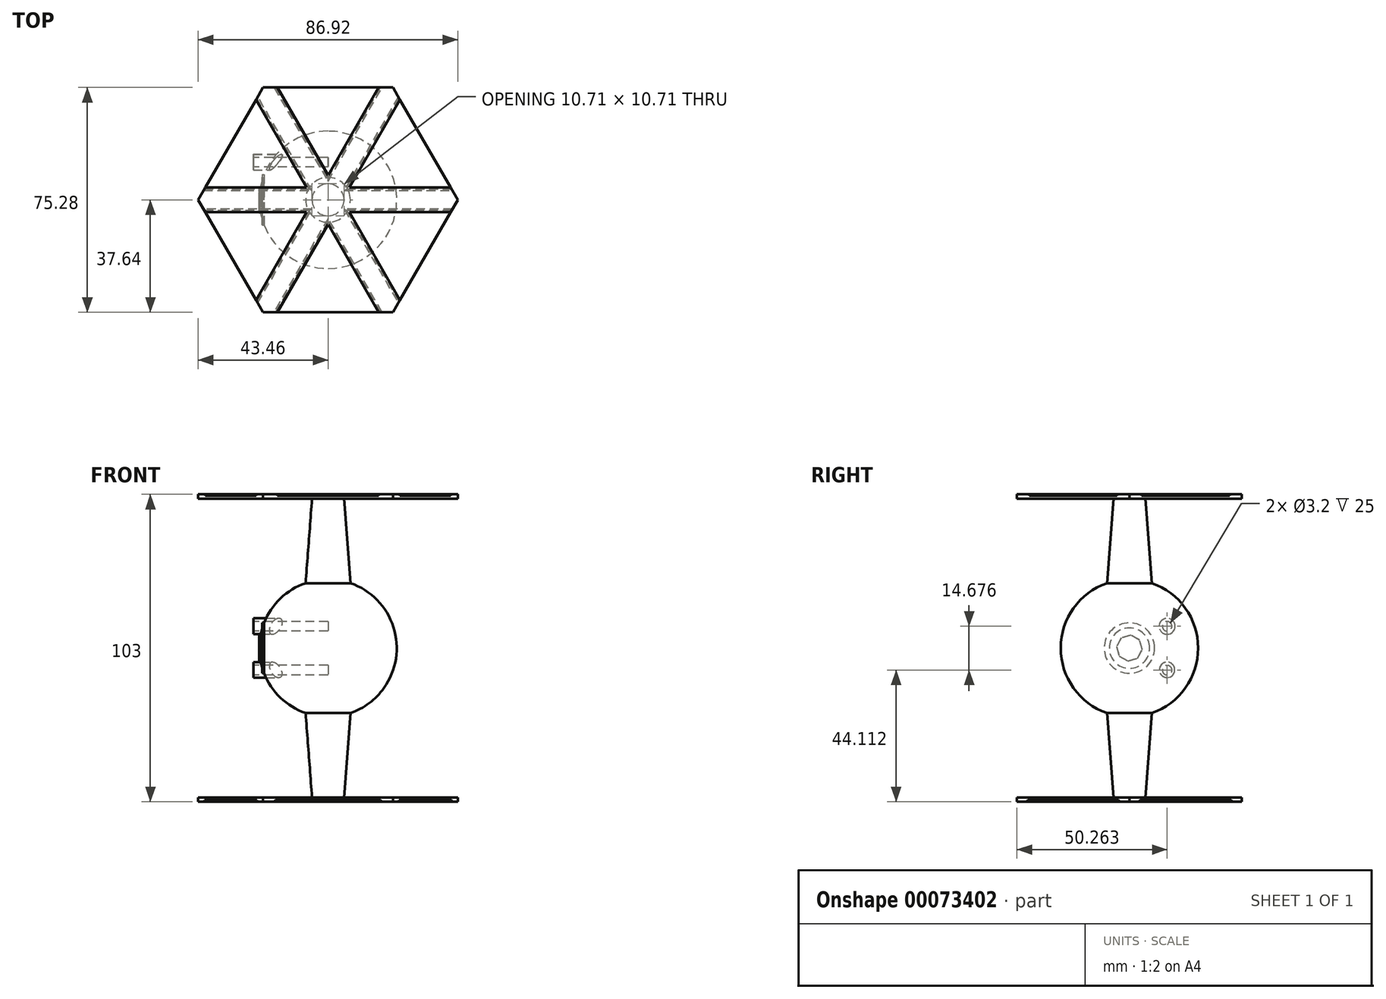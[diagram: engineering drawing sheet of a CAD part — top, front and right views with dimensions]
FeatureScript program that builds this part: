
annotation { "Feature Type Name" : "Feature", "Feature Type Description" : "" }
export const myFeature = defineFeature(function(context is Context, id is Id, definition is map)
    precondition{}
    {
        {
            var Q0;
            Q0=qCreatedBy(makeId("Top.planeOp"),FACE);
            var sketch = newSketch(context, id + "F0", { "sketchPlane" : qUnion([Q0])});
            skArc(sketch, "E0", {"start": v(0, -23.02) * mm, "mid": v(23.02, 0) * mm, "end": v(0, 23.02) * mm});
            skPoint(sketch, "E1.start.orphan", {"position": v(0, 24.97) * mm});
            skLineSegment(sketch, "E2", {"start": v(0, 24.97) * mm, "end": v(0, -23.02) * mm});
            skSolve(sketch);
        }
        {
            var Q0;
            Q0 = qSketchRegion(id + "F0", true);
            var Q1;
            Q1=sQuery(id+"F0.wireOp",EDGE,"E2");
            revolve(context, id + "F1", {"entities" : qUnion([Q0]), "axis" : qUnion([Q1]), "revolveType" : RevolveType.ONE_DIRECTION, "angle" : 180 * degree});
        }
        {
            var Q0;
            Q0=qCreatedBy(makeId("Top.planeOp"),FACE);
            var sketch = newSketch(context, id + "F2", { "sketchPlane" : qUnion([Q0])});
            skCircle(sketch, "E3", {"center": v(0, 0) * mm, "radius": 9.16 * mm});
            skSolve(sketch);
        }
        {
            var Q0;
            Q0=qCreatedBy(makeId("Top.planeOp"),FACE);
            cPlane(context, id + "F3", {"entities" : qUnion([Q0]), "cplaneType" : CPlaneType.OFFSET, "offset" : 50 * mm, "width" : 152.4 * mm, "height" : 152.4 * mm});
        }
        {
            var Q0;
            Q0=qCreatedBy(id+"F3.planeOp",FACE);
            var sketch = newSketch(context, id + "F4", { "sketchPlane" : qUnion([Q0])});
            skCircle(sketch, "E4", {"center": v(0, 0) * mm, "radius": 5.35 * mm});
            skSolve(sketch);
        }
        {
            var Q1;
            Q1=makeQuery(id+"F4.imprint","IMPRINT",FACE,{"disambiguationData":[TD([[makeQuery(id+"F4.imprint","IMPRINT",EDGE,{"derivedFrom":sQuery(id+"F4.wireOp",EDGE,"E4")}),1.0]])]});
            var Q2;
            Q2 = qSketchRegion(id + "F2", true);
            loft(context, id + "F5", {"operationType" : NewBodyOperationType.ADD, "sheetProfilesArray" : [{ "sheetProfileEntities" : qUnion([Q1]) }, { "sheetProfileEntities" : qUnion([Q2]) }]});
        }
        {
            var Q0;
            Q0=qCreatedBy(id+"F3.planeOp",FACE);
            var sketch = newSketch(context, id + "F6", { "sketchPlane" : qUnion([Q0])});
            skCircle(sketch, "E5.cCircle", {"center": v(0, 0) * mm, "radius": 37.64 * mm, "construction": true});
            skLineSegment(sketch, "E5.0", {"start": v(21.73, -37.64) * mm, "end": v(-21.73, -37.64) * mm});
            skLineSegment(sketch, "E5.1", {"start": v(-21.73, -37.64) * mm, "end": v(-43.46, 0) * mm});
            skLineSegment(sketch, "E5.2", {"start": v(-43.46, 0) * mm, "end": v(-21.73, 37.64) * mm});
            skLineSegment(sketch, "E5.3", {"start": v(-21.73, 37.64) * mm, "end": v(21.73, 37.64) * mm});
            skLineSegment(sketch, "E5.4", {"start": v(21.73, 37.64) * mm, "end": v(43.46, 0) * mm});
            skLineSegment(sketch, "E5.5", {"start": v(43.46, 0) * mm, "end": v(21.73, -37.64) * mm});
            skPoint(sketch, "E5.0.midPoint", {"position": v(0, -37.64) * mm});
            skSolve(sketch);
        }
        {
            var Q0;
            Q0 = qSketchRegion(id + "F6", true);
            extrude(context, id + "F7", {"entities" : qUnion([Q0]), "operationType" : NewBodyOperationType.ADD, "depth" : 1 * mm});
        }
        {
            var Q0;
            Q0=makeQuery(id+"F7.opExtrude","CAP_FACE",FACE,{"disambiguationData":[OSD([sQuery(id+"F6.wireOp",EDGE,"E5.0"),sQuery(id+"F6.wireOp",EDGE,"E5.1"),sQuery(id+"F6.wireOp",EDGE,"E5.2"),sQuery(id+"F6.wireOp",EDGE,"E5.3"),sQuery(id+"F6.wireOp",EDGE,"E5.4"),sQuery(id+"F6.wireOp",EDGE,"E5.5")])],"isStart":false});
            var sketch = newSketch(context, id + "F8", { "sketchPlane" : qUnion([Q0])});
            skCircle(sketch, "E6.cCircle", {"center": v(0, 0) * mm, "radius": 8.23 * mm, "construction": true});
            skLineSegment(sketch, "E6.0", {"start": v(4.75, -8.23) * mm, "end": v(-4.75, -8.23) * mm});
            skLineSegment(sketch, "E6.1", {"start": v(-4.75, -8.23) * mm, "end": v(-9.5, 0) * mm});
            skLineSegment(sketch, "E6.2", {"start": v(-9.5, 0) * mm, "end": v(-4.75, 8.23) * mm});
            skLineSegment(sketch, "E6.3", {"start": v(-4.75, 8.23) * mm, "end": v(4.75, 8.23) * mm});
            skLineSegment(sketch, "E6.4", {"start": v(4.75, 8.23) * mm, "end": v(9.5, 0) * mm});
            skLineSegment(sketch, "E6.5", {"start": v(9.5, 0) * mm, "end": v(4.75, -8.23) * mm});
            skPoint(sketch, "E6.0.midPoint", {"position": v(0, -8.23) * mm});
            skLineSegment(sketch, "E7", {"start": v(-7.12, 4.11) * mm, "end": v(-24.1, 33.53) * mm});
            skLineSegment(sketch, "E8", {"start": v(-24.1, 33.53) * mm, "end": v(-21.73, 37.64) * mm});
            skLineSegment(sketch, "E9", {"start": v(-21.73, 37.64) * mm, "end": v(-16.98, 37.64) * mm});
            skLineSegment(sketch, "E10", {"start": v(-16.98, 37.64) * mm, "end": v(0, 8.23) * mm});
            skLineSegment(sketch, "E11", {"start": v(0, 8.23) * mm, "end": v(16.98, 37.64) * mm});
            skLineSegment(sketch, "E12", {"start": v(16.98, 37.64) * mm, "end": v(21.73, 37.64) * mm});
            skLineSegment(sketch, "E13", {"start": v(21.73, 37.64) * mm, "end": v(24.1, 33.53) * mm});
            skLineSegment(sketch, "E14", {"start": v(24.1, 33.53) * mm, "end": v(7.12, 4.11) * mm});
            skLineSegment(sketch, "E15", {"start": v(7.12, 4.11) * mm, "end": v(41.09, 4.11) * mm});
            skLineSegment(sketch, "E16", {"start": v(41.09, 4.11) * mm, "end": v(43.46, 0) * mm});
            skLineSegment(sketch, "E17", {"start": v(43.46, 0) * mm, "end": v(41.09, -4.11) * mm});
            skLineSegment(sketch, "E18", {"start": v(41.09, -4.11) * mm, "end": v(7.12, -4.11) * mm});
            skLineSegment(sketch, "E19", {"start": v(7.12, -4.11) * mm, "end": v(24.1, -33.53) * mm});
            skLineSegment(sketch, "E20", {"start": v(24.1, -33.53) * mm, "end": v(21.73, -37.64) * mm});
            skLineSegment(sketch, "E21", {"start": v(21.73, -37.64) * mm, "end": v(16.98, -37.64) * mm});
            skLineSegment(sketch, "E22", {"start": v(16.98, -37.64) * mm, "end": v(0, -8.23) * mm});
            skLineSegment(sketch, "E23", {"start": v(0, -8.23) * mm, "end": v(-16.98, -37.64) * mm});
            skLineSegment(sketch, "E24", {"start": v(-16.98, -37.64) * mm, "end": v(-21.73, -37.64) * mm});
            skLineSegment(sketch, "E25", {"start": v(-21.73, -37.64) * mm, "end": v(-24.1, -33.53) * mm});
            skLineSegment(sketch, "E26", {"start": v(-24.1, -33.53) * mm, "end": v(-7.12, -4.11) * mm});
            skLineSegment(sketch, "E27", {"start": v(-7.12, -4.11) * mm, "end": v(-41.09, -4.11) * mm});
            skLineSegment(sketch, "E28", {"start": v(-41.09, -4.11) * mm, "end": v(-43.46, 0) * mm});
            skLineSegment(sketch, "E29", {"start": v(-43.46, 0) * mm, "end": v(-41.09, 4.11) * mm});
            skLineSegment(sketch, "E30", {"start": v(-41.09, 4.11) * mm, "end": v(-7.12, 4.11) * mm});
            skSolve(sketch);
        }
        {
            var Q0;
            Q0 = qSketchRegion(id + "F8", true);
            extrude(context, id + "F9", {"entities" : qUnion([Q0]), "operationType" : NewBodyOperationType.ADD, "depth" : 0.5 * mm});
        }
        {
            var Q0;
            Q0=makeQuery(id+"F1.opRevolve","SWEPT_BODY",BODY,{"disambiguationData":[OSD([sQuery(id+"F0.wireOp",EDGE,"E0"),sQuery(id+"F0.wireOp",EDGE,"E2")])]});
            var Q1;
            Q1=qCreatedBy(makeId("Top.planeOp"),FACE);
            mirror(context, id + "F10", {"operationType" : NewBodyOperationType.ADD, "entities" : qUnion([Q0]), "mirrorPlane" : qUnion([Q1])});
        }
        {
            var Q0;
            Q0=qCreatedBy(makeId("Right.planeOp"),FACE);
            var sketch = newSketch(context, id + "F11", { "sketchPlane" : qUnion([Q0])});
            skCircle(sketch, "E31", {"center": v(0, 0) * mm, "radius": 8.45 * mm});
            skSolve(sketch);
        }
        {
            var Q0;
            Q0 = qSketchRegion(id + "F11", true);
            extrude(context, id + "F12", {"entities" : qUnion([Q0]), "operationType" : NewBodyOperationType.ADD, "oppositeDirection" : true, "depth" : 22 * mm});
        }
        {
            var Q0;
            Q0=makeQuery(id+"F12.opExtrude","CAP_FACE",FACE,{"disambiguationData":[OSD([sQuery(id+"F11.wireOp",EDGE,"E31")])],"isStart":false});
            var sketch = newSketch(context, id + "F13", { "sketchPlane" : qUnion([Q0])});
            skCircle(sketch, "E32.cCircle", {"center": v(0, 0) * mm, "radius": 4 * mm, "construction": true});
            skLineSegment(sketch, "E32.0", {"start": v(-2.7, -3.39) * mm, "end": v(-4.31, -0.48) * mm});
            skLineSegment(sketch, "E32.1", {"start": v(-4.31, -0.48) * mm, "end": v(-3.39, 2.7) * mm});
            skLineSegment(sketch, "E32.2", {"start": v(-3.39, 2.7) * mm, "end": v(-0.48, 4.31) * mm});
            skLineSegment(sketch, "E32.3", {"start": v(-0.48, 4.31) * mm, "end": v(2.7, 3.39) * mm});
            skLineSegment(sketch, "E32.4", {"start": v(2.7, 3.39) * mm, "end": v(4.31, 0.48) * mm});
            skLineSegment(sketch, "E32.5", {"start": v(4.31, 0.48) * mm, "end": v(3.39, -2.7) * mm});
            skLineSegment(sketch, "E32.6", {"start": v(3.39, -2.7) * mm, "end": v(0.48, -4.31) * mm});
            skLineSegment(sketch, "E32.7", {"start": v(0.48, -4.31) * mm, "end": v(-2.7, -3.39) * mm});
            skPoint(sketch, "E32.0.midPoint", {"position": v(-3.51, -1.93) * mm});
            skLineSegment(sketch, "E33", {"start": v(4.31, 0.48) * mm, "end": v(6.75, 0.48) * mm});
            skLineSegment(sketch, "E34", {"start": v(3.39, -2.7) * mm, "end": v(5.44, -4.02) * mm});
            skLineSegment(sketch, "E35", {"start": v(-2.7, -3.39) * mm, "end": v(-4.18, -5.31) * mm});
            skLineSegment(sketch, "E36", {"start": v(0.48, -4.31) * mm, "end": v(0.48, -6.75) * mm});
            skLineSegment(sketch, "E37", {"start": v(-4.31, -0.48) * mm, "end": v(-6.75, -0.48) * mm});
            skLineSegment(sketch, "E38", {"start": v(-3.39, 2.7) * mm, "end": v(-5.25, 4.26) * mm});
            skLineSegment(sketch, "E39", {"start": v(-0.48, 4.31) * mm, "end": v(-0.48, 6.75) * mm});
            skLineSegment(sketch, "E40", {"start": v(2.7, 3.39) * mm, "end": v(4.08, 5.4) * mm});
            skSolve(sketch);
        }
        {
            var Q0;
            Q0 = qSketchRegion(id + "F13", true);
            extrude(context, id + "F14", {"entities" : qUnion([Q0]), "operationType" : NewBodyOperationType.ADD, "depth" : 1.1 * mm});
        }
        {
            var Q0;
            Q0=qCreatedBy(makeId("Right.planeOp"),FACE);
            var sketch = newSketch(context, id + "F15", { "sketchPlane" : qUnion([Q0])});
            skCircle(sketch, "E41", {"center": v(12.62, 7.29) * mm, "radius": 2.67 * mm});
            skCircle(sketch, "E42", {"center": v(12.62, -7.29) * mm, "radius": 2.58 * mm});
            skLineSegment(sketch, "E43", {"start": v(12.62, 7.29) * mm, "end": v(0, 0) * mm, "construction": true});
            skLineSegment(sketch, "E44", {"start": v(0, 0) * mm, "end": v(12.62, -7.29) * mm, "construction": true});
            skLineSegment(sketch, "E45", {"start": v(12.62, 7.29) * mm, "end": v(12.62, -7.29) * mm, "construction": true});
            skSolve(sketch);
        }
        {
            var Q0;
            Q0 = qSketchRegion(id + "F15", true);
            extrude(context, id + "F16", {"entities" : qUnion([Q0]), "operationType" : NewBodyOperationType.ADD, "oppositeDirection" : true, "depth" : 25 * mm});
        }
        {
            var Q0;
            Q0=makeQuery(id+"F16.opExtrude","CAP_FACE",FACE,{"disambiguationData":[OSD([sQuery(id+"F15.wireOp",EDGE,"E41")])],"isStart":false});
            var sketch = newSketch(context, id + "F17", { "sketchPlane" : qUnion([Q0])});
            skCircle(sketch, "E46", {"center": v(-12.62, 7.29) * mm, "radius": 1.6 * mm});
            skCircle(sketch, "E47", {"center": v(-12.62, -7.39) * mm, "radius": 1.6 * mm});
            skLineSegment(sketch, "E48", {"start": v(-14.22, 7.29) * mm, "end": v(-11.02, 7.29) * mm, "construction": true});
            skLineSegment(sketch, "E49", {"start": v(-11.03, -7.49) * mm, "end": v(-14.22, -7.39) * mm});
            skSolve(sketch);
        }
        {
            var Q0;
            Q0 = qSketchRegion(id + "F17", true);
            extrude(context, id + "F18", {"entities" : qUnion([Q0]), "operationType" : NewBodyOperationType.REMOVE, "oppositeDirection" : true, "depth" : 25 * mm});
        }
        {
            var Q0;
            Q0=makeQuery(id+"F10.opPattern","COPY",EDGE,{"derivedFrom":makeQuery(id+"F9.opExtrude","CAP_EDGE",EDGE,{"disambiguationData":[OSD([sQuery(id+"F8.wireOp",EDGE,"E27")])],"isStart":false}),"instanceName":"1"});
            var Q1;
            Q1=makeQuery(id+"F10.opPattern","COPY",EDGE,{"derivedFrom":makeQuery(id+"F9.opExtrude","CAP_EDGE",EDGE,{"disambiguationData":[OSD([sQuery(id+"F8.wireOp",EDGE,"E26")])],"isStart":false}),"instanceName":"1"});
            var Q2;
            Q2=makeQuery(id+"F10.opPattern","COPY",EDGE,{"derivedFrom":makeQuery(id+"F9.opExtrude","CAP_EDGE",EDGE,{"disambiguationData":[OSD([sQuery(id+"F8.wireOp",EDGE,"E23")])],"isStart":false}),"instanceName":"1"});
            var Q3;
            Q3=makeQuery(id+"F10.opPattern","COPY",EDGE,{"derivedFrom":makeQuery(id+"F9.opExtrude","CAP_EDGE",EDGE,{"disambiguationData":[OSD([sQuery(id+"F8.wireOp",EDGE,"E22")])],"isStart":false}),"instanceName":"1"});
            var Q4;
            Q4=makeQuery(id+"F10.opPattern","COPY",EDGE,{"derivedFrom":makeQuery(id+"F9.opExtrude","CAP_EDGE",EDGE,{"disambiguationData":[OSD([sQuery(id+"F8.wireOp",EDGE,"E19")])],"isStart":false}),"instanceName":"1"});
            var Q5;
            Q5=makeQuery(id+"F10.opPattern","COPY",EDGE,{"derivedFrom":makeQuery(id+"F9.opExtrude","CAP_EDGE",EDGE,{"disambiguationData":[OSD([sQuery(id+"F8.wireOp",EDGE,"E18")])],"isStart":false}),"instanceName":"1"});
            var Q6;
            Q6=makeQuery(id+"F10.opPattern","COPY",EDGE,{"derivedFrom":makeQuery(id+"F9.opExtrude","CAP_EDGE",EDGE,{"disambiguationData":[OSD([sQuery(id+"F8.wireOp",EDGE,"E15")])],"isStart":false}),"instanceName":"1"});
            var Q7;
            Q7=makeQuery(id+"F10.opPattern","COPY",EDGE,{"derivedFrom":makeQuery(id+"F9.opExtrude","CAP_EDGE",EDGE,{"disambiguationData":[OSD([sQuery(id+"F8.wireOp",EDGE,"E14")])],"isStart":false}),"instanceName":"1"});
            var Q8;
            Q8=makeQuery(id+"F10.opPattern","COPY",EDGE,{"derivedFrom":makeQuery(id+"F9.opExtrude","CAP_EDGE",EDGE,{"disambiguationData":[OSD([sQuery(id+"F8.wireOp",EDGE,"E11")])],"isStart":false}),"instanceName":"1"});
            var Q9;
            Q9=makeQuery(id+"F10.opPattern","COPY",EDGE,{"derivedFrom":makeQuery(id+"F9.opExtrude","CAP_EDGE",EDGE,{"disambiguationData":[OSD([sQuery(id+"F8.wireOp",EDGE,"E10")])],"isStart":false}),"instanceName":"1"});
            var Q10;
            Q10=makeQuery(id+"F10.opPattern","COPY",EDGE,{"derivedFrom":makeQuery(id+"F9.opExtrude","CAP_EDGE",EDGE,{"disambiguationData":[OSD([sQuery(id+"F8.wireOp",EDGE,"E7")])],"isStart":false}),"instanceName":"1"});
            var Q11;
            Q11=makeQuery(id+"F10.opPattern","COPY",EDGE,{"derivedFrom":makeQuery(id+"F9.opExtrude","CAP_EDGE",EDGE,{"disambiguationData":[OSD([sQuery(id+"F8.wireOp",EDGE,"E30")])],"isStart":false}),"instanceName":"1"});
            chamfer(context, id + "F19", {"entities" : qUnion([Q0, Q1, Q2, Q3, Q4, Q5, Q6, Q7, Q8, Q9, Q10, Q11]), "width" : 1 * mm, "tangentPropagation" : true});
        }
    });
